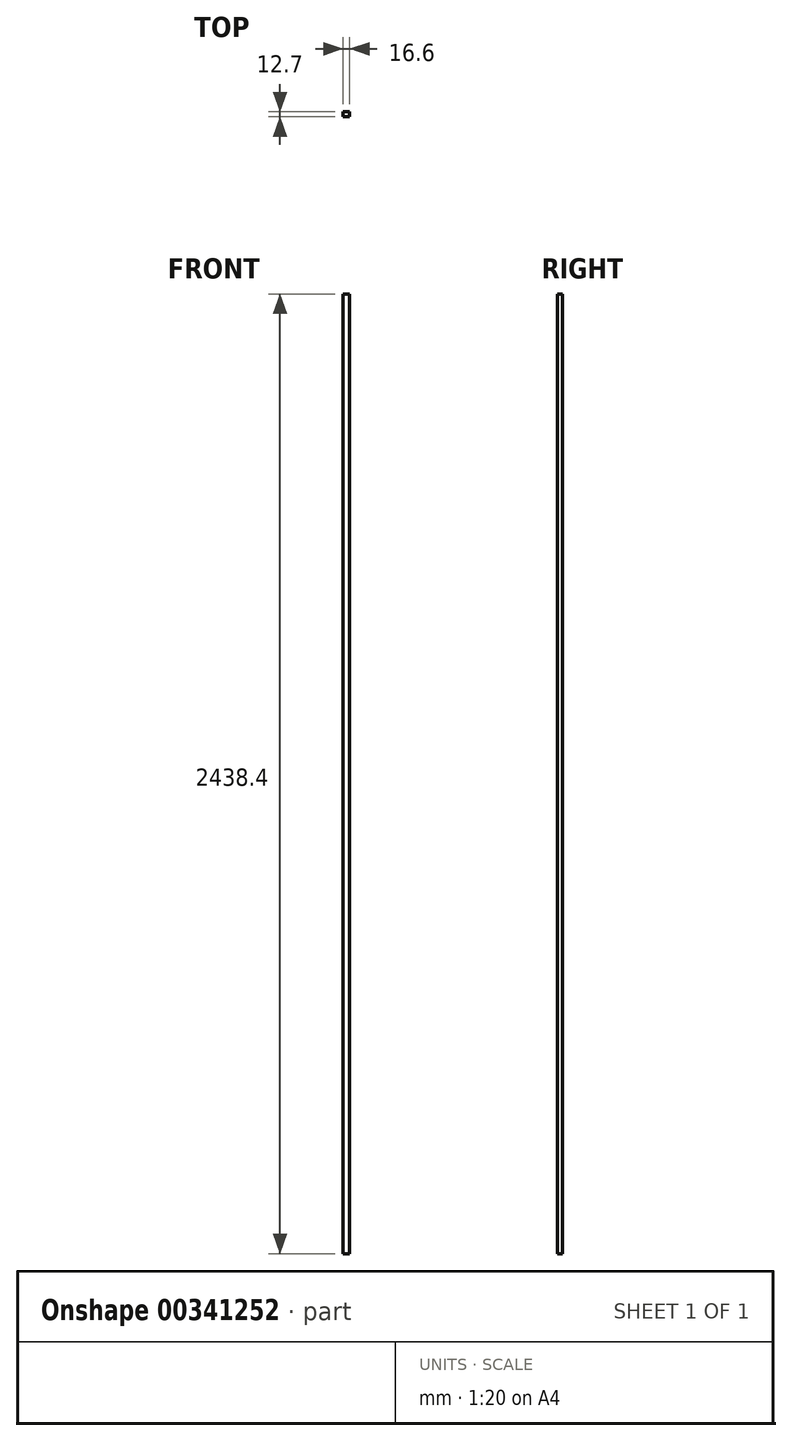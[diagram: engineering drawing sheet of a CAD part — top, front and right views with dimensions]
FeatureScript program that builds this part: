
annotation { "Feature Type Name" : "Feature", "Feature Type Description" : "" }
export const myFeature = defineFeature(function(context is Context, id is Id, definition is map)
    precondition{}
    {
        {
            var Q0;
            Q0=qCreatedBy(makeId("Front.planeOp"),FACE);
            var sketch = newSketch(context, id + "F0", { "sketchPlane" : qUnion([Q0])});
            skLineSegment(sketch, "E0.bottom", {"start": v(-8.3, 1219.2) * mm, "end": v(8.3, 1219.2) * mm});
            skLineSegment(sketch, "E0.top", {"start": v(-8.3, -1219.2) * mm, "end": v(8.3, -1219.2) * mm});
            skLineSegment(sketch, "E0.left", {"start": v(-8.3, 1219.2) * mm, "end": v(-8.3, -1219.2) * mm});
            skLineSegment(sketch, "E0.right", {"start": v(8.3, 1219.2) * mm, "end": v(8.3, -1219.2) * mm});
            skPoint(sketch, "E0.middle", {"position": v(0, 0) * mm});
            skSolve(sketch);
        }
        {
            var Q0;
            Q0=makeQuery(id+"F0.imprint","IMPRINT",FACE,{"disambiguationData":[TD([[makeQuery(id+"F0.imprint","IMPRINT",EDGE,{"derivedFrom":sQuery(id+"F0.wireOp",EDGE,"E0.bottom")}),-1.0]])]});
            extrude(context, id + "F1", {"entities" : qUnion([Q0]), "depth" : 12.7 * mm});
        }
    });
